# Revit family: BENCH_EQUIPMENT
name_source: partatom
category: Furniture
units: mm (PartAtom-declared; Revit-internal decimal feet)

## family parameters
Always vertical = Yes
Cut with Voids When Loaded = No
OmniClass Number = 23.40.20.00
OmniClass Title = General Furniture and Specialties
Room Calculation Point = No
Shared = No
Work Plane-Based = No

## types (24) — shared parameters
CER = No
CUTOUT_CENTER = No
CUTOUT_CENTER_CHECK = No
CUTOUT_SIDES = No
CUTOUT_SIDES_CHECK = No
MARINE_EDGE = No
Manufacturer = IBR Innovasystem
URL = https://ibr-innovasystem.com
WT_MATERIAL = Plástico, blanco opaco
WT_THICK = 16 mm  [stored 0.0524934 ft]
zero-valued in all types: Default Elevation

## per-type parameters (varying)
| type | Depth | Description | LOW_TAG | Length | WTheight_nominal | WTheight_real |
| EQB-15759 | 750 mm  [stored 2.46063 ft] | Equipment Bench (no columns) 1500x750x900 | No | 1500 mm  [stored 4.92126 ft] | 900 mm  [stored 2.95276 ft] | 884 mm  [stored 2.90026 ft] |
| EQB-15909 | 900 mm  [stored 2.95276 ft] | Equipment Bench (no columns) 1500x900x900 | No | 1500 mm  [stored 4.92126 ft] | 900 mm  [stored 2.95276 ft] | 884 mm  [stored 2.90026 ft] |
| EQB-15609 | 600 mm  [stored 1.9685 ft] | Equipment Bench (no columns) 1500x600x900 | No | 1500 mm  [stored 4.92126 ft] | 900 mm  [stored 2.95276 ft] | 884 mm  [stored 2.90026 ft] |
| EQB-15757 | 750 mm  [stored 2.46063 ft] | Equipment Bench (no columns) 1500x750x750 | Yes | 1500 mm  [stored 4.92126 ft] | 750 mm  [stored 2.46063 ft] | 734 mm  [stored 2.40814 ft] |
| EQB-15907 | 900 mm  [stored 2.95276 ft] | Equipment Bench (no columns) 1500x900x750 | Yes | 1500 mm  [stored 4.92126 ft] | 750 mm  [stored 2.46063 ft] | 734 mm  [stored 2.40814 ft] |
| EQB-15607 | 600 mm  [stored 1.9685 ft] | Equipment Bench (no columns) 1500x600x750 | Yes | 1500 mm  [stored 4.92126 ft] | 750 mm  [stored 2.46063 ft] | 734 mm  [stored 2.40814 ft] |
| EQB-12759 | 750 mm  [stored 2.46063 ft] | Equipment Bench (no columns) 1200x750x900 | No | 1200 mm  [stored 3.93701 ft] | 900 mm  [stored 2.95276 ft] | 884 mm  [stored 2.90026 ft] |
| EQB-12909 | 900 mm  [stored 2.95276 ft] | Equipment Bench (no columns) 1200x900x900 | No | 1200 mm  [stored 3.93701 ft] | 900 mm  [stored 2.95276 ft] | 884 mm  [stored 2.90026 ft] |
| EQB-12609 | 600 mm  [stored 1.9685 ft] | Equipment Bench (no columns) 1200x600x900 | No | 1200 mm  [stored 3.93701 ft] | 900 mm  [stored 2.95276 ft] | 884 mm  [stored 2.90026 ft] |
| EQB-12757 | 750 mm  [stored 2.46063 ft] | Equipment Bench (no columns) 1200x750x750 | Yes | 1200 mm  [stored 3.93701 ft] | 750 mm  [stored 2.46063 ft] | 734 mm  [stored 2.40814 ft] |
| EQB-12907 | 900 mm  [stored 2.95276 ft] | Equipment Bench (no columns) 1200x900x750 | Yes | 1200 mm  [stored 3.93701 ft] | 750 mm  [stored 2.46063 ft] | 734 mm  [stored 2.40814 ft] |
| EQB-12607 | 600 mm  [stored 1.9685 ft] | Equipment Bench (no columns) 1200x600x750 | Yes | 1200 mm  [stored 3.93701 ft] | 750 mm  [stored 2.46063 ft] | 734 mm  [stored 2.40814 ft] |
| EQB-09759 | 750 mm  [stored 2.46063 ft] | Equipment Bench (no columns) 900x750x900 | No | 900 mm  [stored 2.95276 ft] | 900 mm  [stored 2.95276 ft] | 884 mm  [stored 2.90026 ft] |
| EQB-09909 | 900 mm  [stored 2.95276 ft] | Equipment Bench (no columns) 900x900x900 | No | 900 mm  [stored 2.95276 ft] | 900 mm  [stored 2.95276 ft] | 884 mm  [stored 2.90026 ft] |
| EQB-09609 | 600 mm  [stored 1.9685 ft] | Equipment Bench (no columns) 900x600x900 | No | 900 mm  [stored 2.95276 ft] | 900 mm  [stored 2.95276 ft] | 884 mm  [stored 2.90026 ft] |
| EQB-09757 | 750 mm  [stored 2.46063 ft] | Equipment Bench (no columns) 900x750x750 | Yes | 900 mm  [stored 2.95276 ft] | 750 mm  [stored 2.46063 ft] | 734 mm  [stored 2.40814 ft] |
| EQB-09907 | 900 mm  [stored 2.95276 ft] | Equipment Bench (no columns) 900x900x750 | Yes | 900 mm  [stored 2.95276 ft] | 750 mm  [stored 2.46063 ft] | 734 mm  [stored 2.40814 ft] |
| EQB-09607 | 600 mm  [stored 1.9685 ft] | Equipment Bench (no columns) 900x600x750 | Yes | 900 mm  [stored 2.95276 ft] | 750 mm  [stored 2.46063 ft] | 734 mm  [stored 2.40814 ft] |
| EQB-75759 | 750 mm  [stored 2.46063 ft] | Equipment Bench (no columns) 750x750x900 | No | 750 mm  [stored 2.46063 ft] | 900 mm  [stored 2.95276 ft] | 884 mm  [stored 2.90026 ft] |
| EQB-75909 | 900 mm  [stored 2.95276 ft] | Equipment Bench (no columns) 750x900x900 | No | 750 mm  [stored 2.46063 ft] | 900 mm  [stored 2.95276 ft] | 884 mm  [stored 2.90026 ft] |
| EQB-75609 | 600 mm  [stored 1.9685 ft] | Equipment Bench (no columns) 750x600x900 | No | 750 mm  [stored 2.46063 ft] | 900 mm  [stored 2.95276 ft] | 884 mm  [stored 2.90026 ft] |
| EQB-75757 | 750 mm  [stored 2.46063 ft] | Equipment Bench (no columns) 750x750x750 | Yes | 750 mm  [stored 2.46063 ft] | 750 mm  [stored 2.46063 ft] | 734 mm  [stored 2.40814 ft] |
| EQB-75907 | 900 mm  [stored 2.95276 ft] | Equipment Bench (no columns) 750x900x750 | Yes | 750 mm  [stored 2.46063 ft] | 750 mm  [stored 2.46063 ft] | 734 mm  [stored 2.40814 ft] |
| EQB-75607 | 600 mm  [stored 1.9685 ft] | Equipment Bench (no columns) 750x600x750 | Yes | 750 mm  [stored 2.46063 ft] | 750 mm  [stored 2.46063 ft] | 734 mm  [stored 2.40814 ft] |

note: [stored X ft] marks values corroborated as IEEE doubles in the binary element streams (Revit-internal decimal feet)

## geometry (parser evidence)
native form markers: Sweep x53
no freeform markers — native parametric forms only
